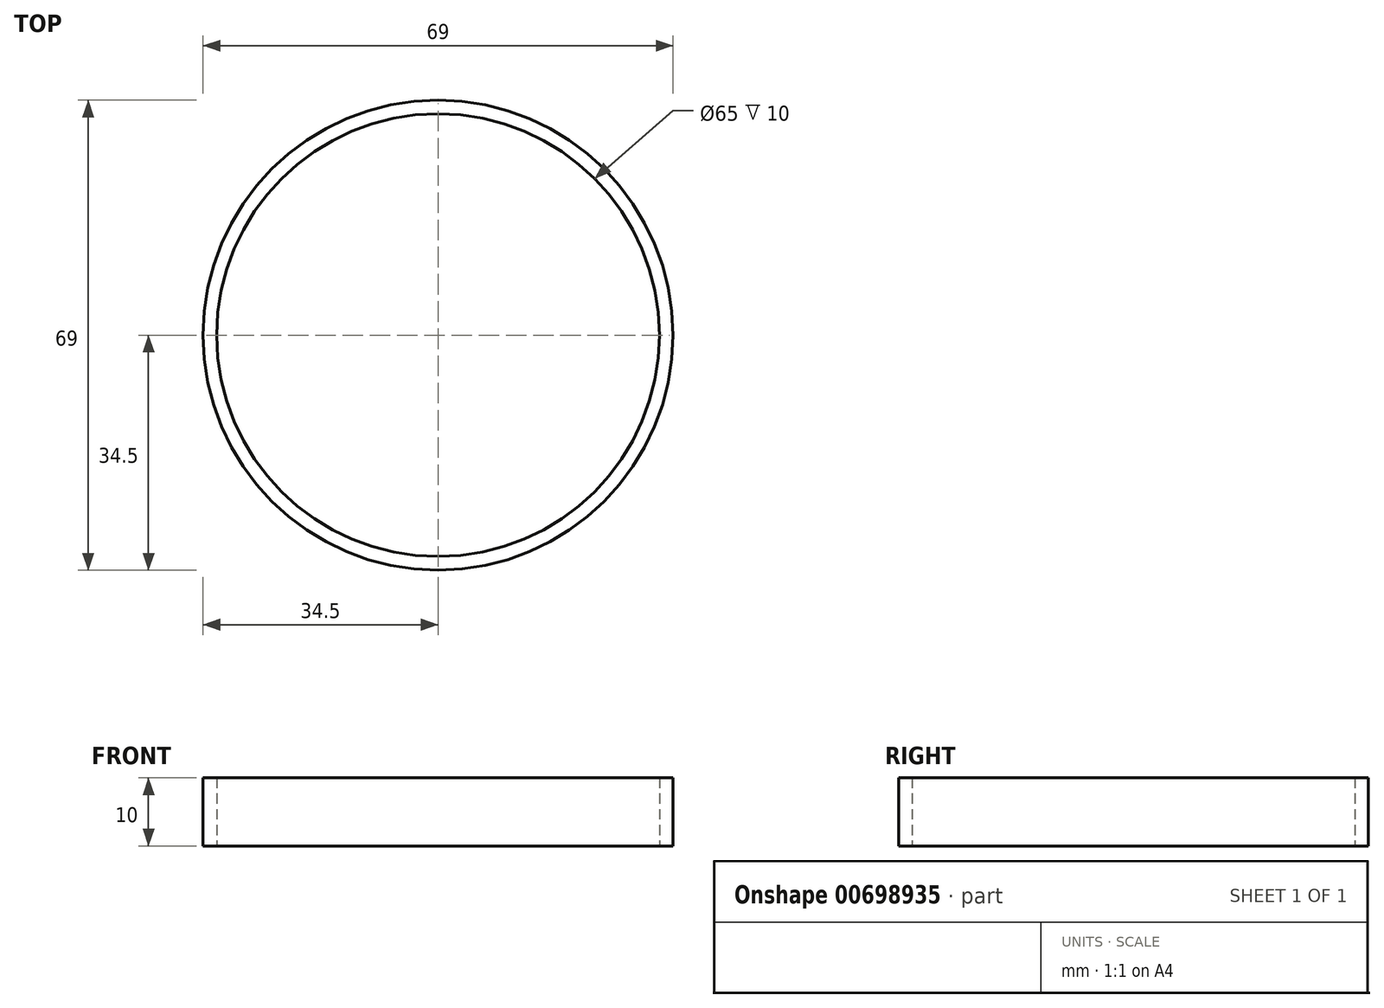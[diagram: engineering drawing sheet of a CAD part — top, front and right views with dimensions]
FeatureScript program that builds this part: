
annotation { "Feature Type Name" : "Feature", "Feature Type Description" : "" }
export const myFeature = defineFeature(function(context is Context, id is Id, definition is map)
    precondition{}
    {
        {
            var Q0;
            Q0=qCreatedBy(makeId("Top.planeOp"),FACE);
            var sketch = newSketch(context, id + "F0", { "sketchPlane" : qUnion([Q0])});
            skCircle(sketch, "E0", {"center": v(0, 0) * mm, "radius": 32.5 * mm});
            skCircle(sketch, "E1", {"center": v(0, 0) * mm, "radius": 34.5 * mm});
            skSolve(sketch);
        }
        {
            var Q0;
            Q0=makeQuery(id+"F0.imprint","IMPRINT",FACE,{"disambiguationData":[TD([[makeQuery(id+"F0.imprint","IMPRINT",EDGE,{"derivedFrom":sQuery(id+"F0.wireOp",EDGE,"E0")}),-1.0]])]});
            extrude(context, id + "F1", {"entities" : qUnion([Q0]), "depth" : 10 * mm, "offsetDistance" : 25 * mm});
        }
    });
